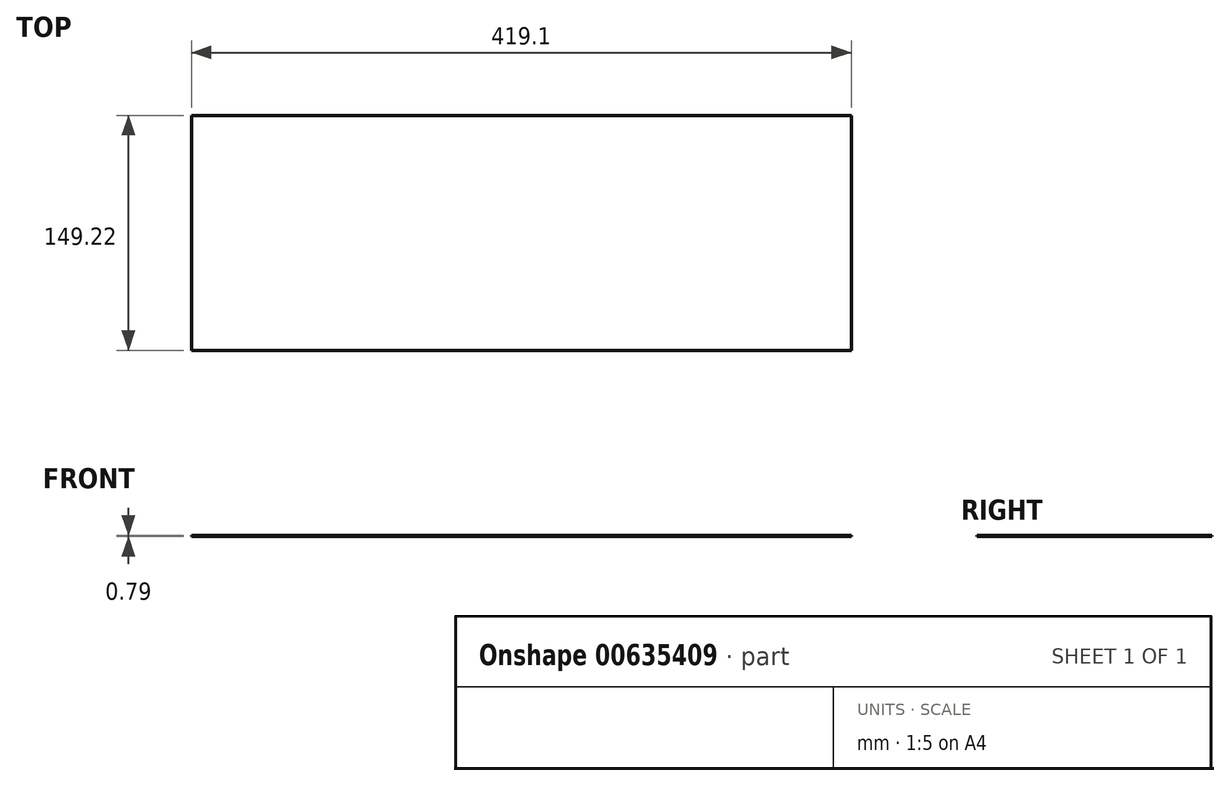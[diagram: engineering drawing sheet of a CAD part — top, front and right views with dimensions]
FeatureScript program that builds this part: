
annotation { "Feature Type Name" : "Feature", "Feature Type Description" : "" }
export const myFeature = defineFeature(function(context is Context, id is Id, definition is map)
    precondition{}
    {
        {
            var Q0;
            Q0=qCreatedBy(makeId("Top.planeOp"),FACE);
            var sketch = newSketch(context, id + "F0", { "sketchPlane" : qUnion([Q0])});
            skLineSegment(sketch, "E0.bottom", {"start": v(209.55, -74.61) * mm, "end": v(-209.55, -74.61) * mm});
            skLineSegment(sketch, "E0.top", {"start": v(209.55, 74.61) * mm, "end": v(-209.55, 74.61) * mm});
            skLineSegment(sketch, "E0.left", {"start": v(209.55, -74.61) * mm, "end": v(209.55, 74.61) * mm});
            skLineSegment(sketch, "E0.right", {"start": v(-209.55, -74.61) * mm, "end": v(-209.55, 74.61) * mm});
            skPoint(sketch, "E0.middle", {"position": v(0, 0) * mm});
            skSolve(sketch);
        }
        {
            var Q0;
            Q0=makeQuery(id+"F0.imprint","IMPRINT",FACE,{"disambiguationData":[TD([[makeQuery(id+"F0.imprint","IMPRINT",EDGE,{"derivedFrom":sQuery(id+"F0.wireOp",EDGE,"E0.bottom")}),-1.0]])]});
            extrude(context, id + "F1", {"entities" : qUnion([Q0]), "depth" : 0.8 * mm});
        }
    });
